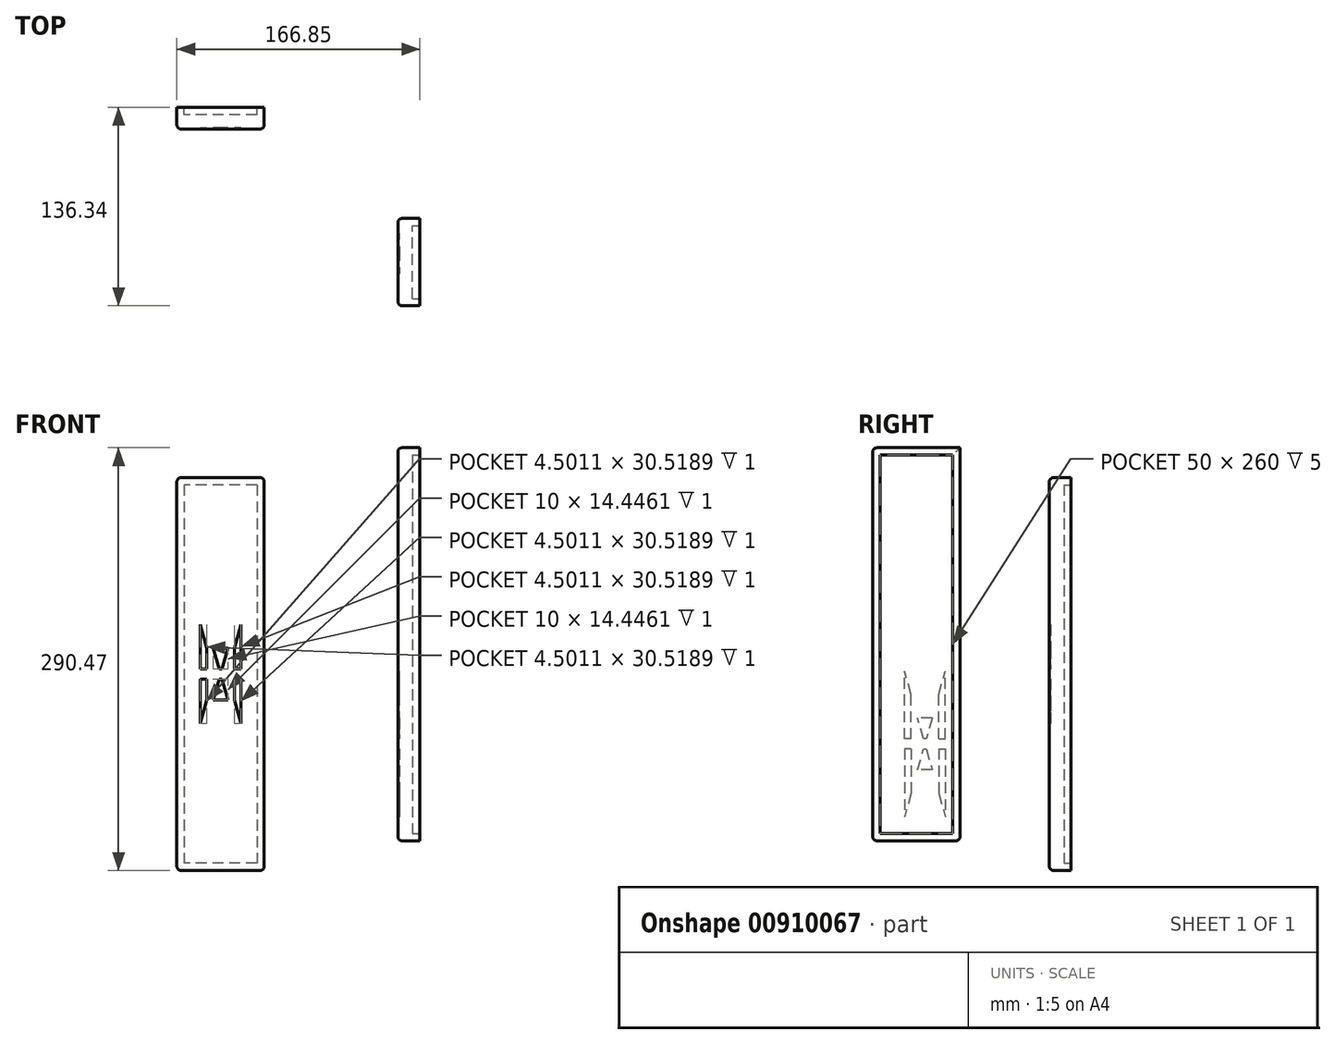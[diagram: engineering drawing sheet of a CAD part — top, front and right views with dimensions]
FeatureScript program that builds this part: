
annotation { "Feature Type Name" : "Feature", "Feature Type Description" : "" }
export const myFeature = defineFeature(function(context is Context, id is Id, definition is map)
    precondition{}
    {
        {
            var Q0;
            Q0=qCreatedBy(makeId("Front.planeOp"),FACE);
            var sketch = newSketch(context, id + "F0", { "sketchPlane" : qUnion([Q0])});
            skPoint(sketch, "E0.middle", {"position": v(0, 0) * mm});
            skLineSegment(sketch, "E1.bottom", {"start": v(-151.85, 109.1) * mm, "end": v(-91.85, 109.1) * mm});
            skLineSegment(sketch, "E1.top", {"start": v(-151.85, -160.9) * mm, "end": v(-91.85, -160.9) * mm});
            skLineSegment(sketch, "E1.left", {"start": v(-151.85, 109.1) * mm, "end": v(-151.85, -160.9) * mm});
            skLineSegment(sketch, "E1.right", {"start": v(-91.85, 109.1) * mm, "end": v(-91.85, -160.9) * mm});
            skSolve(sketch);
        }
        {
            var Q0;
            Q0=qCreatedBy(makeId("Right.planeOp"),FACE);
            var sketch = newSketch(context, id + "F1", { "sketchPlane" : qUnion([Q0])});
            skLineSegment(sketch, "E2.bottom", {"start": v(-136.34, 129.58) * mm, "end": v(-76.34, 129.58) * mm});
            skLineSegment(sketch, "E2.top", {"start": v(-136.34, -140.42) * mm, "end": v(-76.34, -140.42) * mm});
            skLineSegment(sketch, "E2.left", {"start": v(-136.34, 129.58) * mm, "end": v(-136.34, -140.42) * mm});
            skLineSegment(sketch, "E2.right", {"start": v(-76.34, 129.58) * mm, "end": v(-76.34, -140.42) * mm});
            skSolve(sketch);
        }
        {
            var Q0;
            Q0=qSketchRegion(id+"F0",true);
            extrude(context, id + "F2", {"entities" : qUnion([Q0]), "depth" : 15 * mm, "offsetDistance" : 25 * mm});
        }
        {
            var Q0;
            Q0=makeQuery(id+"F0.imprint","IMPRINT",FACE,{"disambiguationData":[TD([[makeQuery(id+"F0.imprint","IMPRINT",EDGE,{"derivedFrom":sQuery(id+"F0.wireOp",EDGE,"E1.bottom")}),-1.0]])]});
            var sketch = newSketch(context, id + "F3", { "sketchPlane" : qUnion([Q0])});
            skLineSegment(sketch, "E3.bottom", {"start": v(-96.85, 104.1) * mm, "end": v(-146.85, 104.1) * mm});
            skLineSegment(sketch, "E3.top", {"start": v(-96.85, -155.9) * mm, "end": v(-146.85, -155.9) * mm});
            skLineSegment(sketch, "E3.left", {"start": v(-96.85, 104.1) * mm, "end": v(-96.85, -155.9) * mm});
            skLineSegment(sketch, "E3.right", {"start": v(-146.85, 104.1) * mm, "end": v(-146.85, -155.9) * mm});
            skSolve(sketch);
        }
        {
            var Q0;
            Q0=makeQuery(id+"F3.imprint","IMPRINT",FACE,{"disambiguationData":[TD([[makeQuery(id+"F3.imprint","IMPRINT",EDGE,{"derivedFrom":sQuery(id+"F3.wireOp",EDGE,"E3.bottom")}),1.0]])]});
            extrude(context, id + "F4", {"entities" : qUnion([Q0]), "operationType" : NewBodyOperationType.ADD, "depth" : -5 * mm, "offsetDistance" : 25 * mm});
        }
        {
            var Q0;
            Q0=qSketchRegion(id+"F1",true);
            extrude(context, id + "F5", {"entities" : qUnion([Q0]), "depth" : 15 * mm, "offsetDistance" : 25 * mm});
        }
        {
            var Q0;
            Q0=makeQuery(id+"F5.opExtrude","CAP_FACE",FACE,{"disambiguationData":[OSD([sQuery(id+"F1.wireOp",EDGE,"E2.bottom"),sQuery(id+"F1.wireOp",EDGE,"E2.top"),sQuery(id+"F1.wireOp",EDGE,"E2.left"),sQuery(id+"F1.wireOp",EDGE,"E2.right")])],"isStart":false});
            var sketch = newSketch(context, id + "F6", { "sketchPlane" : qUnion([Q0])});
            skLineSegment(sketch, "E4.bottom", {"start": v(-131.34, 124.58) * mm, "end": v(-81.34, 124.58) * mm});
            skLineSegment(sketch, "E4.top", {"start": v(-131.34, -135.42) * mm, "end": v(-81.34, -135.42) * mm});
            skLineSegment(sketch, "E4.left", {"start": v(-131.34, 124.58) * mm, "end": v(-131.34, -135.42) * mm});
            skLineSegment(sketch, "E4.right", {"start": v(-81.34, 124.58) * mm, "end": v(-81.34, -135.42) * mm});
            skSolve(sketch);
        }
        {
            var Q0;
            Q0=makeQuery(id+"F6.imprint","IMPRINT",FACE,{"disambiguationData":[TD([[makeQuery(id+"F6.imprint","IMPRINT",EDGE,{"derivedFrom":sQuery(id+"F6.wireOp",EDGE,"E4.bottom")}),-1.0]])]});
            extrude(context, id + "F7", {"entities" : qUnion([Q0]), "operationType" : NewBodyOperationType.REMOVE, "oppositeDirection" : true, "depth" : 5 * mm, "offsetDistance" : 25 * mm});
        }
        {
            var Q0;
            Q0=makeQuery(id+"F4.opExtrude","CAP_FACE",FACE,{"disambiguationData":[OSD([sQuery(id+"F3.wireOp",EDGE,"E3.bottom"),sQuery(id+"F3.wireOp",EDGE,"E3.top"),sQuery(id+"F3.wireOp",EDGE,"E3.left"),sQuery(id+"F3.wireOp",EDGE,"E3.right")])],"isStart":false});
            var sketch = newSketch(context, id + "F8", { "sketchPlane" : qUnion([Q0])});
            skLineSegment(sketch, "E5.bottom", {"start": v(133.85, -150.9) * mm, "end": v(109.85, -150.9) * mm});
            skLineSegment(sketch, "E5.top", {"start": v(133.85, 99.1) * mm, "end": v(109.85, 99.1) * mm});
            skLineSegment(sketch, "E5.left", {"start": v(133.85, -150.9) * mm, "end": v(133.85, 99.1) * mm});
            skLineSegment(sketch, "E5.right", {"start": v(109.85, -150.9) * mm, "end": v(109.85, 99.1) * mm});
            skEllipse(sketch, "E6", {"center": v(121.85, -25.9) * mm, "majorRadius": 25 * mm, "minorRadius": 20 * mm, "majorAxis": v(0, 1)});
            skSolve(sketch);
        }
        {
            var Q0;
            Q0=makeQuery(id+"F8.imprint","IMPRINT",FACE,{"disambiguationData":[TD([[makeQuery(id+"F8.imprint","IMPRINT",EDGE,{"derivedFrom":sQuery(id+"F8.wireOp",EDGE,"E5.bottom")}),-1.0]])]});
            var Q1;
            {var subQ0=sQuery(id+"F8.wireOp",EDGE,"E5.right");var subQ1=sQuery(id+"F8.wireOp",EDGE,"E5.top");var subQ2=makeQuery(id+"F8.imprint","INTERSECT",VERTEX,{"derivedFrom":[subQ1,subQ0]});Q1=makeQuery(id+"F8.imprint","IMPRINT",FACE,{"disambiguationData":[TD([[makeQuery(id+"F8.imprint","IMPRINT",EDGE,{"disambiguationData":[TD([[subQ2,1.0]])],"derivedFrom":subQ1}),1.0]])]});}
            var Q2;
            {var subQ0=sQuery(id+"F8.wireOp",EDGE,"E5.left");var subQ1=sQuery(id+"F8.wireOp",EDGE,"E5.top");var subQ2=makeQuery(id+"F8.imprint","INTERSECT",VERTEX,{"derivedFrom":[subQ1,subQ0]});Q2=makeQuery(id+"F8.imprint","IMPRINT",FACE,{"disambiguationData":[TD([[makeQuery(id+"F8.imprint","IMPRINT",EDGE,{"disambiguationData":[TD([[subQ2,-1.0]])],"derivedFrom":subQ1}),1.0]])]});}
            var Q3;
            {var subQ0=sQuery(id+"F8.wireOp",EDGE,"jjR4p86R-AGvj-MJNc-cVGU-iWlVXVb1kiAX");var subQ1=sQuery(id+"F8.wireOp",EDGE,"E5.right");var subQ2=makeQuery(id+"F8.imprint","INTERSECT",VERTEX,{"derivedFrom":[subQ1,subQ0]});Q3=makeQuery(id+"F8.imprint","IMPRINT",FACE,{"disambiguationData":[TD([[makeQuery(id+"F8.imprint","IMPRINT",EDGE,{"disambiguationData":[TD([[subQ2,-1.0]])],"derivedFrom":subQ1}),-1.0]])]});}
            var Q4;
            {var subQ0=sQuery(id+"F8.wireOp",EDGE,"jjR4p86R-AGvj-MJNc-cVGU-iWlVXVb1kiAX");var subQ1=sQuery(id+"F8.wireOp",EDGE,"E5.left");var subQ2=makeQuery(id+"F8.imprint","INTERSECT",VERTEX,{"derivedFrom":[subQ1,subQ0]});Q4=makeQuery(id+"F8.imprint","IMPRINT",FACE,{"disambiguationData":[TD([[makeQuery(id+"F8.imprint","IMPRINT",EDGE,{"disambiguationData":[TD([[subQ2,-1.0]])],"derivedFrom":subQ1}),1.0]])]});}
            var Q5;
            {var subQ0=sQuery(id+"F8.wireOp",EDGE,"jjR4p86R-AGvj-MJNc-cVGU-iWlVXVb1kiAX");var subQ1=sQuery(id+"F8.wireOp",EDGE,"E5.left");var subQ2=makeQuery(id+"F8.imprint","INTERSECT",VERTEX,{"derivedFrom":[subQ1,subQ0]});Q5=makeQuery(id+"F8.imprint","IMPRINT",FACE,{"disambiguationData":[TD([[makeQuery(id+"F8.imprint","IMPRINT",EDGE,{"disambiguationData":[TD([[subQ2,-1.0]])],"derivedFrom":subQ1}),-1.0]])]});}
            var Q6;
            {var subQ0=sQuery(id+"F8.wireOp",EDGE,"E6");var subQ1=sQuery(id+"F8.wireOp",EDGE,"E5.left");var subQ2=makeQuery(id+"F8.imprint","INTERSECT",VERTEX,{"disambiguationData":[OD(0.0)],"derivedFrom":[subQ1,subQ0]});Q6=makeQuery(id+"F8.imprint","IMPRINT",FACE,{"disambiguationData":[TD([[makeQuery(id+"F8.imprint","IMPRINT",EDGE,{"disambiguationData":[TD([[subQ2,-1.0]])],"derivedFrom":subQ1}),-1.0]])]});}
            var Q7;
            {var subQ0=sQuery(id+"F8.wireOp",EDGE,"E6");var subQ1=sQuery(id+"F8.wireOp",EDGE,"E5.left");var subQ2=makeQuery(id+"F8.imprint","INTERSECT",VERTEX,{"disambiguationData":[OD(0.0)],"derivedFrom":[subQ1,subQ0]});Q7=makeQuery(id+"F8.imprint","IMPRINT",FACE,{"disambiguationData":[TD([[makeQuery(id+"F8.imprint","IMPRINT",EDGE,{"disambiguationData":[TD([[subQ2,-1.0]])],"derivedFrom":subQ1}),1.0]])]});}
            var Q8;
            {var subQ0=sQuery(id+"F8.wireOp",EDGE,"E6");var subQ1=sQuery(id+"F8.wireOp",EDGE,"E5.right");var subQ2=makeQuery(id+"F8.imprint","INTERSECT",VERTEX,{"disambiguationData":[OD(0.0)],"derivedFrom":[subQ1,subQ0]});Q8=makeQuery(id+"F8.imprint","IMPRINT",FACE,{"disambiguationData":[TD([[makeQuery(id+"F8.imprint","IMPRINT",EDGE,{"disambiguationData":[TD([[subQ2,-1.0]])],"derivedFrom":subQ1}),-1.0]])]});}
            var Q9;
            {var subQ0=sQuery(id+"F8.wireOp",EDGE,"E6");var subQ1=sQuery(id+"F8.wireOp",EDGE,"E5.right");var subQ2=makeQuery(id+"F8.imprint","INTERSECT",VERTEX,{"disambiguationData":[OD(0.0)],"derivedFrom":[subQ1,subQ0]});Q9=makeQuery(id+"F8.imprint","IMPRINT",FACE,{"disambiguationData":[TD([[makeQuery(id+"F8.imprint","IMPRINT",EDGE,{"disambiguationData":[TD([[subQ2,-1.0]])],"derivedFrom":subQ1}),1.0]])]});}
            var Q10;
            {var subQ0=sQuery(id+"F8.wireOp",EDGE,"jjR4p86R-AGvj-MJNc-cVGU-iWlVXVb1kiAX");var subQ1=sQuery(id+"F8.wireOp",EDGE,"E5.right");var subQ2=makeQuery(id+"F8.imprint","INTERSECT",VERTEX,{"derivedFrom":[subQ1,subQ0]});Q10=makeQuery(id+"F8.imprint","IMPRINT",FACE,{"disambiguationData":[TD([[makeQuery(id+"F8.imprint","IMPRINT",EDGE,{"disambiguationData":[TD([[subQ2,-1.0]])],"derivedFrom":subQ1}),1.0]])]});}
            extrude(context, id + "F9", {"entities" : qUnion([Q0, Q1, Q2, Q3, Q4, Q5, Q6, Q7, Q8, Q9, Q10]), "operationType" : NewBodyOperationType.REMOVE, "oppositeDirection" : true, "depth" : 10 * mm, "offsetDistance" : 25 * mm});
        }
        {
            var Q0;
            Q0=makeQuery(id+"F2.opExtrude","CAP_EDGE",EDGE,{"disambiguationData":[OSD([sQuery(id+"F0.wireOp",EDGE,"E1.bottom")])],"isStart":false});
            var Q1;
            Q1=makeQuery(id+"F2.opExtrude","SWEPT_EDGE",EDGE,{"disambiguationData":[OSD([sQuery(id+"F0.wireOp",EDGE,"E1.bottom"),sQuery(id+"F0.wireOp",EDGE,"E1.left")])]});
            var Q2;
            Q2=makeQuery(id+"F2.opExtrude","SWEPT_EDGE",EDGE,{"disambiguationData":[OSD([sQuery(id+"F0.wireOp",EDGE,"E1.bottom"),sQuery(id+"F0.wireOp",EDGE,"E1.right")])]});
            var Q3;
            Q3=makeQuery(id+"F2.opExtrude","CAP_EDGE",EDGE,{"disambiguationData":[OSD([sQuery(id+"F0.wireOp",EDGE,"E1.right")])],"isStart":false});
            var Q4;
            Q4=makeQuery(id+"F2.opExtrude","CAP_EDGE",EDGE,{"disambiguationData":[OSD([sQuery(id+"F0.wireOp",EDGE,"E1.left")])],"isStart":false});
            var Q5;
            Q5=makeQuery(id+"F2.opExtrude","CAP_EDGE",EDGE,{"disambiguationData":[OSD([sQuery(id+"F0.wireOp",EDGE,"E1.top")])],"isStart":false});
            var Q6;
            Q6=makeQuery(id+"F2.opExtrude","SWEPT_EDGE",EDGE,{"disambiguationData":[OSD([sQuery(id+"F0.wireOp",EDGE,"E1.top"),sQuery(id+"F0.wireOp",EDGE,"E1.left")])]});
            var Q7;
            Q7=makeQuery(id+"F2.opExtrude","SWEPT_EDGE",EDGE,{"disambiguationData":[OSD([sQuery(id+"F0.wireOp",EDGE,"E1.top"),sQuery(id+"F0.wireOp",EDGE,"E1.right")])]});
            fillet(context, id + "F10", {"entities" : qUnion([Q0, Q1, Q2, Q3, Q4, Q5, Q6, Q7]), "radius" : 3 * mm, "tangentPropagation" : true, "allowEdgeOverflow" : false});
        }
        {
            var Q0;
            Q0=makeQuery(id+"F5.opExtrude","SWEPT_EDGE",EDGE,{"disambiguationData":[OSD([sQuery(id+"F1.wireOp",EDGE,"E2.bottom"),sQuery(id+"F1.wireOp",EDGE,"E2.left")])]});
            var Q1;
            Q1=makeQuery(id+"F5.opExtrude","CAP_EDGE",EDGE,{"disambiguationData":[OSD([sQuery(id+"F1.wireOp",EDGE,"E2.bottom")])],"isStart":true});
            var Q2;
            Q2=makeQuery(id+"F5.opExtrude","CAP_EDGE",EDGE,{"disambiguationData":[OSD([sQuery(id+"F1.wireOp",EDGE,"E2.left")])],"isStart":true});
            var Q3;
            Q3=makeQuery(id+"F5.opExtrude","CAP_EDGE",EDGE,{"disambiguationData":[OSD([sQuery(id+"F1.wireOp",EDGE,"E2.right")])],"isStart":true});
            var Q4;
            Q4=makeQuery(id+"F5.opExtrude","CAP_EDGE",EDGE,{"disambiguationData":[OSD([sQuery(id+"F1.wireOp",EDGE,"E2.top")])],"isStart":true});
            var Q5;
            Q5=makeQuery(id+"F5.opExtrude","SWEPT_EDGE",EDGE,{"disambiguationData":[OSD([sQuery(id+"F1.wireOp",EDGE,"E2.top"),sQuery(id+"F1.wireOp",EDGE,"E2.right")])]});
            var Q6;
            Q6=makeQuery(id+"F5.opExtrude","SWEPT_EDGE",EDGE,{"disambiguationData":[OSD([sQuery(id+"F1.wireOp",EDGE,"E2.top"),sQuery(id+"F1.wireOp",EDGE,"E2.left")])]});
            fillet(context, id + "F11", {"entities" : qUnion([Q0, Q1, Q2, Q3, Q4, Q5, Q6]), "radius" : 3 * mm, "tangentPropagation" : true, "allowEdgeOverflow" : false});
        }
        {
            var Q0;
            Q0=makeQuery(id+"F5.opExtrude","CAP_FACE",FACE,{"disambiguationData":[OSD([sQuery(id+"F1.wireOp",EDGE,"E2.bottom"),sQuery(id+"F1.wireOp",EDGE,"E2.top"),sQuery(id+"F1.wireOp",EDGE,"E2.left"),sQuery(id+"F1.wireOp",EDGE,"E2.right")])],"isStart":true});
            var sketch = newSketch(context, id + "F12", { "sketchPlane" : qUnion([Q0])});
            skLineSegment(sketch, "E7", {"start": v(95.46, -56.01) * mm, "end": v(105.46, -56.01) * mm});
            skLineSegment(sketch, "E8", {"start": v(95.46, -91.72) * mm, "end": v(105.46, -91.72) * mm});
            skLineSegment(sketch, "E9", {"start": v(90.96, -39.94) * mm, "end": v(86.46, -23.87) * mm});
            skLineSegment(sketch, "E10", {"start": v(90.96, -107.8) * mm, "end": v(86.46, -123.87) * mm});
            skLineSegment(sketch, "E11", {"start": v(109.96, -107.8) * mm, "end": v(114.46, -123.87) * mm});
            skLineSegment(sketch, "E12", {"start": v(109.96, -39.94) * mm, "end": v(114.46, -23.87) * mm});
            skLineSegment(sketch, "E13", {"start": v(95.46, -56.01) * mm, "end": v(99.5, -70.46) * mm});
            skLineSegment(sketch, "E14", {"start": v(99.5, -70.46) * mm, "end": v(101.41, -70.46) * mm});
            skLineSegment(sketch, "E15", {"start": v(101.41, -70.46) * mm, "end": v(105.46, -56.01) * mm});
            skLineSegment(sketch, "E16", {"start": v(105.46, -91.72) * mm, "end": v(101.41, -77.27) * mm});
            skLineSegment(sketch, "E17", {"start": v(101.41, -77.27) * mm, "end": v(99.5, -77.27) * mm});
            skLineSegment(sketch, "E18", {"start": v(99.5, -77.27) * mm, "end": v(95.46, -91.72) * mm});
            skLineSegment(sketch, "E19", {"start": v(90.96, -77.27) * mm, "end": v(86.46, -77.27) * mm});
            skLineSegment(sketch, "E20", {"start": v(109.96, -77.27) * mm, "end": v(114.46, -77.27) * mm});
            skLineSegment(sketch, "E21", {"start": v(109.96, -70.46) * mm, "end": v(114.46, -70.46) * mm});
            skLineSegment(sketch, "E22", {"start": v(109.96, -70.46) * mm, "end": v(109.96, -39.94) * mm});
            skLineSegment(sketch, "E23", {"start": v(109.96, -77.27) * mm, "end": v(109.96, -107.8) * mm});
            skLineSegment(sketch, "E24", {"start": v(90.96, -70.46) * mm, "end": v(86.46, -70.46) * mm});
            skLineSegment(sketch, "E25", {"start": v(90.96, -70.46) * mm, "end": v(90.96, -39.94) * mm});
            skLineSegment(sketch, "E26", {"start": v(90.96, -77.27) * mm, "end": v(90.96, -107.8) * mm});
            skLineSegment(sketch, "E27", {"start": v(86.46, -70.46) * mm, "end": v(86.46, -23.87) * mm});
            skLineSegment(sketch, "E28", {"start": v(86.46, -77.27) * mm, "end": v(86.46, -123.87) * mm});
            skLineSegment(sketch, "E29", {"start": v(114.46, -70.46) * mm, "end": v(114.46, -23.87) * mm});
            skLineSegment(sketch, "E30", {"start": v(114.46, -77.27) * mm, "end": v(114.46, -123.87) * mm});
            skSolve(sketch);
        }
        {
            var Q0;
            Q0=makeQuery(id+"F12.imprint","IMPRINT",FACE,{"disambiguationData":[TD([[makeQuery(id+"F12.imprint","IMPRINT",EDGE,{"derivedFrom":sQuery(id+"F12.wireOp",EDGE,"E7")}),-1.0]])]});
            var Q1;
            Q1=makeQuery(id+"F12.imprint","IMPRINT",FACE,{"disambiguationData":[TD([[makeQuery(id+"F12.imprint","IMPRINT",EDGE,{"derivedFrom":sQuery(id+"F12.wireOp",EDGE,"E9")}),1.0]])]});
            var Q2;
            Q2=makeQuery(id+"F12.imprint","IMPRINT",FACE,{"disambiguationData":[TD([[makeQuery(id+"F12.imprint","IMPRINT",EDGE,{"derivedFrom":sQuery(id+"F12.wireOp",EDGE,"E12")}),-1.0]])]});
            var Q3;
            Q3=makeQuery(id+"F12.imprint","IMPRINT",FACE,{"disambiguationData":[TD([[makeQuery(id+"F12.imprint","IMPRINT",EDGE,{"derivedFrom":sQuery(id+"F12.wireOp",EDGE,"E11")}),1.0]])]});
            var Q4;
            Q4=makeQuery(id+"F12.imprint","IMPRINT",FACE,{"disambiguationData":[TD([[makeQuery(id+"F12.imprint","IMPRINT",EDGE,{"derivedFrom":sQuery(id+"F12.wireOp",EDGE,"E8")}),1.0]])]});
            var Q5;
            Q5=makeQuery(id+"F12.imprint","IMPRINT",FACE,{"disambiguationData":[TD([[makeQuery(id+"F12.imprint","IMPRINT",EDGE,{"derivedFrom":sQuery(id+"F12.wireOp",EDGE,"E10")}),-1.0]])]});
            extrude(context, id + "F13", {"entities" : qUnion([Q0, Q1, Q2, Q3, Q4, Q5]), "operationType" : NewBodyOperationType.REMOVE, "oppositeDirection" : true, "depth" : 1 * mm, "offsetDistance" : 25 * mm});
        }
        {
            var Q0;
            Q0=makeQuery(id+"F2.opExtrude","CAP_FACE",FACE,{"disambiguationData":[OSD([sQuery(id+"F0.wireOp",EDGE,"E1.bottom"),sQuery(id+"F0.wireOp",EDGE,"E1.top"),sQuery(id+"F0.wireOp",EDGE,"E1.left"),sQuery(id+"F0.wireOp",EDGE,"E1.right")])],"isStart":false});
            var sketch = newSketch(context, id + "F14", { "sketchPlane" : qUnion([Q0])});
            skLineSegment(sketch, "E31", {"start": v(-126.85, -8.04) * mm, "end": v(-116.85, -8.04) * mm});
            skLineSegment(sketch, "E32", {"start": v(-126.85, -43.74) * mm, "end": v(-116.85, -43.74) * mm});
            skLineSegment(sketch, "E33", {"start": v(-126.85, -8.04) * mm, "end": v(-122.8, -22.48) * mm});
            skLineSegment(sketch, "E34", {"start": v(-122.8, -22.48) * mm, "end": v(-120.9, -22.48) * mm});
            skLineSegment(sketch, "E35", {"start": v(-120.9, -22.48) * mm, "end": v(-116.85, -8.04) * mm});
            skLineSegment(sketch, "E36", {"start": v(-116.85, -43.74) * mm, "end": v(-120.9, -29.3) * mm});
            skLineSegment(sketch, "E37", {"start": v(-120.9, -29.3) * mm, "end": v(-122.8, -29.3) * mm});
            skLineSegment(sketch, "E38", {"start": v(-122.8, -29.3) * mm, "end": v(-126.85, -43.74) * mm});
            skLineSegment(sketch, "E39", {"start": v(-131.35, -43.74) * mm, "end": v(-131.35, -29.3) * mm});
            skLineSegment(sketch, "E40", {"start": v(-131.35, -8.04) * mm, "end": v(-131.35, -22.48) * mm});
            skLineSegment(sketch, "E41", {"start": v(-131.35, -22.48) * mm, "end": v(-135.85, -22.48) * mm});
            skLineSegment(sketch, "E42", {"start": v(-135.85, 8.04) * mm, "end": v(-131.35, -8.04) * mm});
            skLineSegment(sketch, "E43", {"start": v(-112.35, -8.04) * mm, "end": v(-112.35, -22.48) * mm});
            skLineSegment(sketch, "E44", {"start": v(-107.85, -22.48) * mm, "end": v(-112.35, -22.48) * mm});
            skLineSegment(sketch, "E45", {"start": v(-112.35, -43.74) * mm, "end": v(-112.35, -29.3) * mm});
            skLineSegment(sketch, "E46", {"start": v(-107.85, -59.82) * mm, "end": v(-112.35, -43.74) * mm});
            skLineSegment(sketch, "E47", {"start": v(-107.85, -59.82) * mm, "end": v(-107.85, -29.3) * mm});
            skLineSegment(sketch, "E48", {"start": v(-112.35, -29.3) * mm, "end": v(-107.85, -29.3) * mm});
            skLineSegment(sketch, "E49", {"start": v(-135.85, -29.3) * mm, "end": v(-135.85, -59.82) * mm});
            skLineSegment(sketch, "E50", {"start": v(-135.85, 8.04) * mm, "end": v(-135.85, -22.48) * mm});
            skLineSegment(sketch, "E51", {"start": v(-107.85, 8.04) * mm, "end": v(-112.35, -8.04) * mm});
            skLineSegment(sketch, "E52", {"start": v(-107.85, -22.48) * mm, "end": v(-107.85, 8.04) * mm});
            skLineSegment(sketch, "E53", {"start": v(-135.85, -29.3) * mm, "end": v(-131.35, -29.3) * mm});
            skLineSegment(sketch, "E54", {"start": v(-131.35, -43.74) * mm, "end": v(-135.85, -59.82) * mm});
            skSolve(sketch);
        }
        {
            var Q0;
            Q0=makeQuery(id+"F14.imprint","IMPRINT",FACE,{"disambiguationData":[TD([[makeQuery(id+"F14.imprint","IMPRINT",EDGE,{"derivedFrom":sQuery(id+"F14.wireOp",EDGE,"E39")}),1.0]])]});
            var Q1;
            Q1=makeQuery(id+"F14.imprint","IMPRINT",FACE,{"disambiguationData":[TD([[makeQuery(id+"F14.imprint","IMPRINT",EDGE,{"derivedFrom":sQuery(id+"F14.wireOp",EDGE,"E32")}),1.0]])]});
            var Q2;
            Q2=makeQuery(id+"F14.imprint","IMPRINT",FACE,{"disambiguationData":[TD([[makeQuery(id+"F14.imprint","IMPRINT",EDGE,{"derivedFrom":sQuery(id+"F14.wireOp",EDGE,"E45")}),-1.0]])]});
            var Q3;
            Q3=makeQuery(id+"F14.imprint","IMPRINT",FACE,{"disambiguationData":[TD([[makeQuery(id+"F14.imprint","IMPRINT",EDGE,{"derivedFrom":sQuery(id+"F14.wireOp",EDGE,"E43")}),1.0]])]});
            var Q4;
            Q4=makeQuery(id+"F14.imprint","IMPRINT",FACE,{"disambiguationData":[TD([[makeQuery(id+"F14.imprint","IMPRINT",EDGE,{"derivedFrom":sQuery(id+"F14.wireOp",EDGE,"E31")}),-1.0]])]});
            var Q5;
            Q5=makeQuery(id+"F14.imprint","IMPRINT",FACE,{"disambiguationData":[TD([[makeQuery(id+"F14.imprint","IMPRINT",EDGE,{"derivedFrom":sQuery(id+"F14.wireOp",EDGE,"E40")}),-1.0]])]});
            extrude(context, id + "F15", {"entities" : qUnion([Q0, Q1, Q2, Q3, Q4, Q5]), "operationType" : NewBodyOperationType.REMOVE, "oppositeDirection" : true, "depth" : 1 * mm, "offsetDistance" : 25 * mm});
        }
    });
